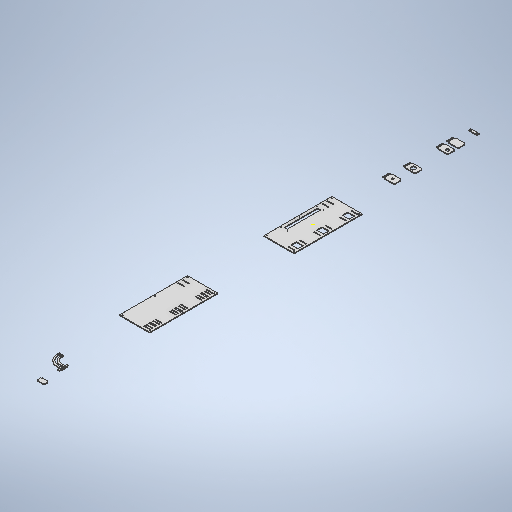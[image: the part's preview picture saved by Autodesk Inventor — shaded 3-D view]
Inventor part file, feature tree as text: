
AUTODESK INVENTOR PART (.ipt)
format: ipt  version: 2025 (Build 290162000, 162)  size: 601,600 bytes
history: native  units: in
note: dims shown in document units (in); Inventor stores cm internally (conversion verified against a paired STEP export)
features: sketch x3, extrude x2
ambient origin geometry x8: Origin, YZ Plane, XZ Plane, XY Plane, X Axis, Y Axis, Z Axis, Center Point
bodies: Solid1 (feature_tree)
feature tree (5):
  sketch  "Sketch1"  dims[d0=7.874in d1=17.7165in]
  extrude  "Extrusion1"  Depth=17.7165in
  extrude  "Extrusion2"  Depth=0.2362in
  sketch  "Sketch2"  dims[d16=1.1811in d21=0.2362in]
  sketch  "Sketch3"  dims[d23=1.5748in d24=0.1969in d29=8.6614in d32=0.2362in d33=0.2362in d36=7.874in d37=17.7165in d40=1.5748in d41=0.1969in d43=0.2362in d44=0.2362in d46=0.4724in d47=1.5748in d51=2.3622in d61=2.3622in d62=2.3622in d63=2.3622in d64=0.5512in d70=0.1969in d72=0.1969in d75=1.5748in d76=0.1969in d79=1.5748in d80=0.1969in d82=2.2047in d83=0.5906in d85=0.2362in d88=1.4173in d89=1.7717in d90=0.1969in d91=0.0in d92=0.1969in d93=1.5748in d94=0.3937in d95=0.3937in d96=2.3622in d99=1.1811in d100=0.7874in d101=0.7874in d102=0.374in d103=0.374in d107=2.4016in d108=1.9685in d109=0.374in d113=1.4961in d114=1.1811in d115=0.1969in d116=0.1969in d117=0.7874in d118=0.1969in d119=0.0in]
